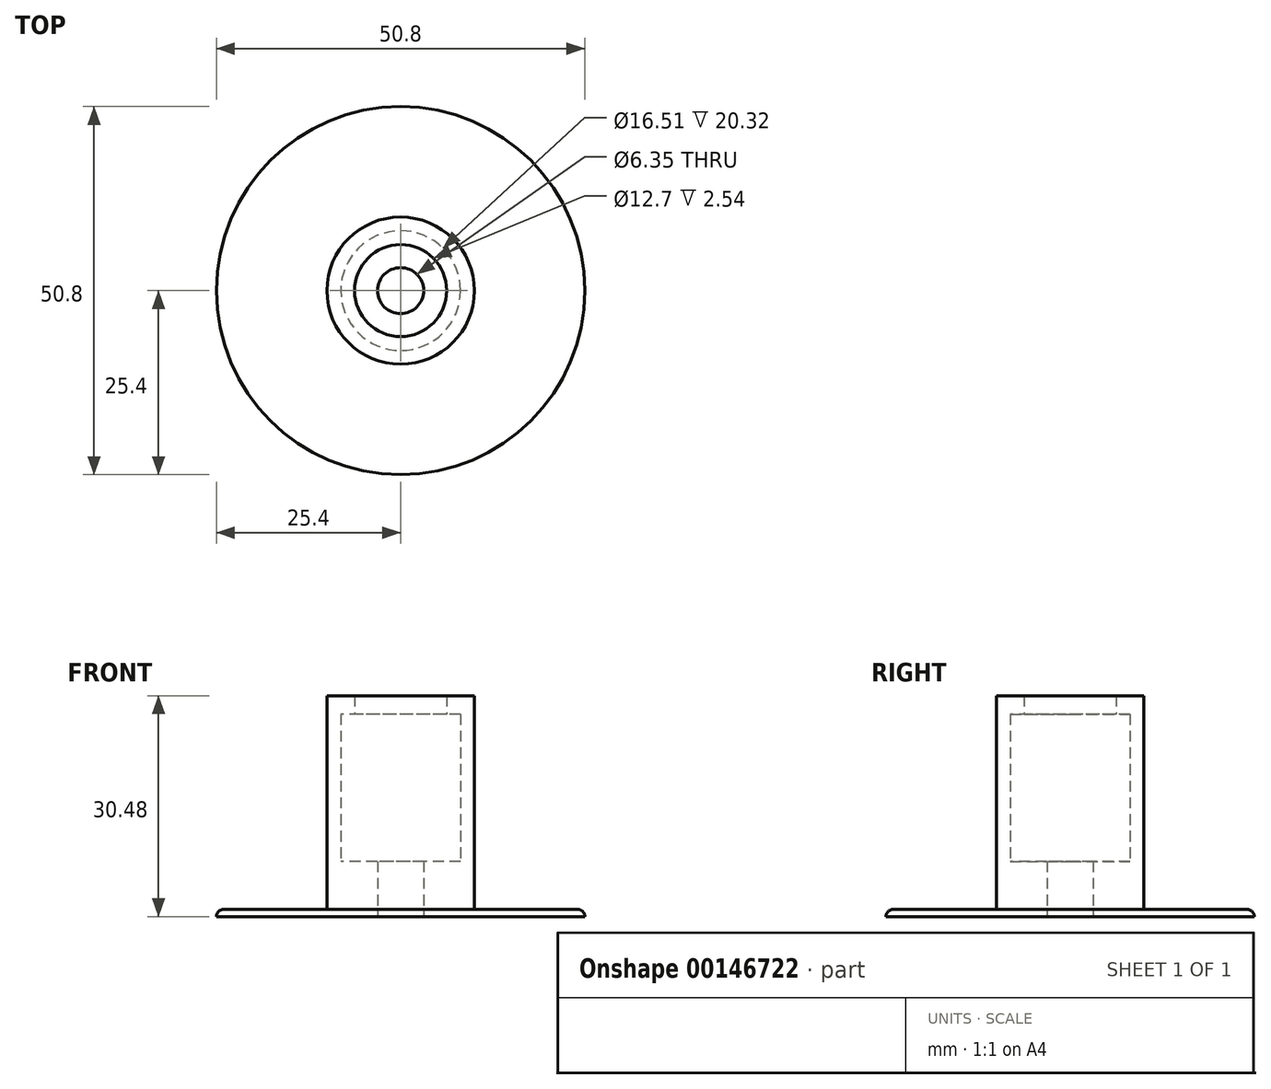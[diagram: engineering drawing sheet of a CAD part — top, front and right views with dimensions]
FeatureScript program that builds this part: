
annotation { "Feature Type Name" : "Feature", "Feature Type Description" : "" }
export const myFeature = defineFeature(function(context is Context, id is Id, definition is map)
    precondition{}
    {
        {
            assignVariable(context, id + "F0", {"name" : "R", "anyValue" : 2});
        }
        {
            var Q0;
            Q0=qCreatedBy(makeId("Top.planeOp"),FACE);
            var sketch = newSketch(context, id + "F1", { "sketchPlane" : qUnion([Q0])});
            skCircle(sketch, "E0", {"center": v(0, 0) * mm, "radius": 25.4 * mm});
            skCircle(sketch, "E1", {"center": v(0, 0) * mm, "radius": 10.16 * mm});
            skSolve(sketch);
        }
        {
            var Q0;
            Q0=makeQuery(id+"F1.imprint","IMPRINT",FACE,{"disambiguationData":[TD([[makeQuery(id+"F1.imprint","IMPRINT",EDGE,{"derivedFrom":sQuery(id+"F1.wireOp",EDGE,"E0")}),1.0]])]});
            var Q1;
            Q1=makeQuery(id+"F1.imprint","IMPRINT",FACE,{"disambiguationData":[TD([[makeQuery(id+"F1.imprint","IMPRINT",EDGE,{"derivedFrom":sQuery(id+"F1.wireOp",EDGE,"E1")}),1.0]])]});
            extrude(context, id + "F2", {"entities" : qUnion([Q0, Q1]), "depth" : (getVariable(context, 'R') / 2) * mm});
        }
        {
            var Q0;
            Q0=makeQuery(id+"F2.opExtrude","CAP_EDGE",EDGE,{"disambiguationData":[OSD([sQuery(id+"F1.wireOp",EDGE,"E0")])],"isStart":false});
            fillet(context, id + "F3", {"entities" : qUnion([Q0]), "radius" : (getVariable(context, 'R') / 2) * mm, "tangentPropagation" : true, "allowEdgeOverflow" : false});
        }
        {
            var Q0;
            Q0=makeQuery(id+"F1.imprint","IMPRINT",FACE,{"disambiguationData":[TD([[makeQuery(id+"F1.imprint","IMPRINT",EDGE,{"derivedFrom":sQuery(id+"F1.wireOp",EDGE,"E1")}),1.0]])]});
            extrude(context, id + "F4", {"entities" : qUnion([Q0]), "operationType" : NewBodyOperationType.ADD, "depth" : 30.48 * mm});
        }
        {
            var Q0;
            Q0=makeQuery(id+"F1.imprint","IMPRINT",FACE,{"disambiguationData":[TD([[makeQuery(id+"F1.imprint","IMPRINT",EDGE,{"derivedFrom":sQuery(id+"F1.wireOp",EDGE,"E0")}),1.0]])]});
            var sketch = newSketch(context, id + "F5", { "sketchPlane" : qUnion([Q0])});
            skCircle(sketch, "E2", {"center": v(0, 0) * mm, "radius": 16.51 * mm});
            skSolve(sketch);
        }
        {
            var Q0;
            Q0=makeQuery(id+"F5.imprint","IMPRINT",FACE,{"disambiguationData":[TD([[makeQuery(id+"F5.imprint","IMPRINT",EDGE,{"derivedFrom":makeQuery(id+"F1.imprint","IMPRINT",EDGE,{"derivedFrom":sQuery(id+"F1.wireOp",EDGE,"E1")})}),1.0]])]});
            var sketch = newSketch(context, id + "F6", { "sketchPlane" : qUnion([Q0])});
            skPoint(sketch, "E3", {"position": v(0, 0) * mm});
            skCircle(sketch, "E4", {"center": v(0, 0) * mm, "radius": 6.35 * mm});
            skLineSegment(sketch, "E5", {"start": v(0, 0) * mm, "end": v(-12.7, 0) * mm});
            skLineSegment(sketch, "E6", {"start": v(0, 0) * mm, "end": v(12.7, 0) * mm});
            skCircle(sketch, "E7", {"center": v(-12.7, 0) * mm, "radius": 2.54 * mm});
            skCircle(sketch, "E8", {"center": v(12.7, 0) * mm, "radius": 2.54 * mm});
            skCircle(sketch, "E9", {"center": v(0, 0) * mm, "radius": 3.18 * mm});
            skCircle(sketch, "E10", {"center": v(0, 0) * mm, "radius": 8.26 * mm});
            skSolve(sketch);
        }
        {
            var Q0;
            Q0=sQuery(id+"F6.wireOp",VERTEX,"E3");
            var Q1;
            Q1=makeQuery(id+"F2.opExtrude","SWEPT_BODY",BODY,{"disambiguationData":[OSD([sQuery(id+"F1.wireOp",EDGE,"E0")])]});
            hole(context, id + "F7", {"style" : HoleStyle.SIMPLE, "endStyle" : HoleEndStyle.THROUGH, "oppositeDirection" : true, "holeDiameter" : 16.5 * mm, "startFromSketch" : true, "locations" : qUnion([Q0]), "scope" : qUnion([Q1]), "isTappedThrough" : true});
        }
        {
            var Q0;
            {var subQ0=sQuery(id+"F6.wireOp",EDGE,"E5");var subQ1=sQuery(id+"F6.wireOp",EDGE,"E4");var subQ2=makeQuery(id+"F6.imprint","INTERSECT",VERTEX,{"derivedFrom":[subQ1,subQ0]});Q0=makeQuery(id+"F6.imprint","IMPRINT",FACE,{"disambiguationData":[TD([[makeQuery(id+"F6.imprint","IMPRINT",EDGE,{"disambiguationData":[TD([[subQ2,-1.0]])],"derivedFrom":subQ1}),1.0]])]});}
            var Q1;
            {var subQ0=sQuery(id+"F6.wireOp",EDGE,"E5");var subQ1=sQuery(id+"F6.wireOp",EDGE,"E4");var subQ2=makeQuery(id+"F6.imprint","INTERSECT",VERTEX,{"derivedFrom":[subQ1,subQ0]});Q1=makeQuery(id+"F6.imprint","IMPRINT",FACE,{"disambiguationData":[TD([[makeQuery(id+"F6.imprint","IMPRINT",EDGE,{"disambiguationData":[TD([[subQ2,1.0]])],"derivedFrom":subQ1}),1.0]])]});}
            var Q2;
            {var subQ0=sQuery(id+"F6.wireOp",EDGE,"E5");var subQ1=sQuery(id+"F6.wireOp",EDGE,"E4");var subQ2=makeQuery(id+"F6.imprint","INTERSECT",VERTEX,{"derivedFrom":[subQ1,subQ0]});Q2=makeQuery(id+"F6.imprint","IMPRINT",FACE,{"disambiguationData":[TD([[makeQuery(id+"F6.imprint","IMPRINT",EDGE,{"disambiguationData":[TD([[subQ2,-1.0]])],"derivedFrom":subQ1}),-1.0]])]});}
            var Q3;
            {var subQ0=sQuery(id+"F6.wireOp",EDGE,"E5");var subQ1=sQuery(id+"F6.wireOp",EDGE,"E4");var subQ2=makeQuery(id+"F6.imprint","INTERSECT",VERTEX,{"derivedFrom":[subQ1,subQ0]});Q3=makeQuery(id+"F6.imprint","IMPRINT",FACE,{"disambiguationData":[TD([[makeQuery(id+"F6.imprint","IMPRINT",EDGE,{"disambiguationData":[TD([[subQ2,1.0]])],"derivedFrom":subQ1}),-1.0]])]});}
            extrude(context, id + "F8", {"entities" : qUnion([Q0, Q1, Q2, Q3]), "operationType" : NewBodyOperationType.ADD, "depth" : 7.62 * mm});
        }
        {
            var Q0;
            {var subQ0=sQuery(id+"F6.wireOp",EDGE,"E5");var subQ1=sQuery(id+"F6.wireOp",EDGE,"E4");var subQ2=makeQuery(id+"F6.imprint","INTERSECT",VERTEX,{"derivedFrom":[subQ1,subQ0]});Q0=makeQuery(id+"F6.imprint","IMPRINT",FACE,{"disambiguationData":[TD([[makeQuery(id+"F6.imprint","IMPRINT",EDGE,{"disambiguationData":[TD([[subQ2,-1.0]])],"derivedFrom":subQ1}),-1.0]])]});}
            var Q1;
            {var subQ0=sQuery(id+"F6.wireOp",EDGE,"E5");var subQ1=sQuery(id+"F6.wireOp",EDGE,"E4");var subQ2=makeQuery(id+"F6.imprint","INTERSECT",VERTEX,{"derivedFrom":[subQ1,subQ0]});Q1=makeQuery(id+"F6.imprint","IMPRINT",FACE,{"disambiguationData":[TD([[makeQuery(id+"F6.imprint","IMPRINT",EDGE,{"disambiguationData":[TD([[subQ2,1.0]])],"derivedFrom":subQ1}),-1.0]])]});}
            extrude(context, id + "F9", {"entities" : qUnion([Q0, Q1]), "operationType" : NewBodyOperationType.ADD, "depth" : 30.48 * mm, "hasSecondDirection" : true, "secondDirectionOppositeDirection" : false, "secondDirectionDepth" : 27.94 * mm});
        }
    });
